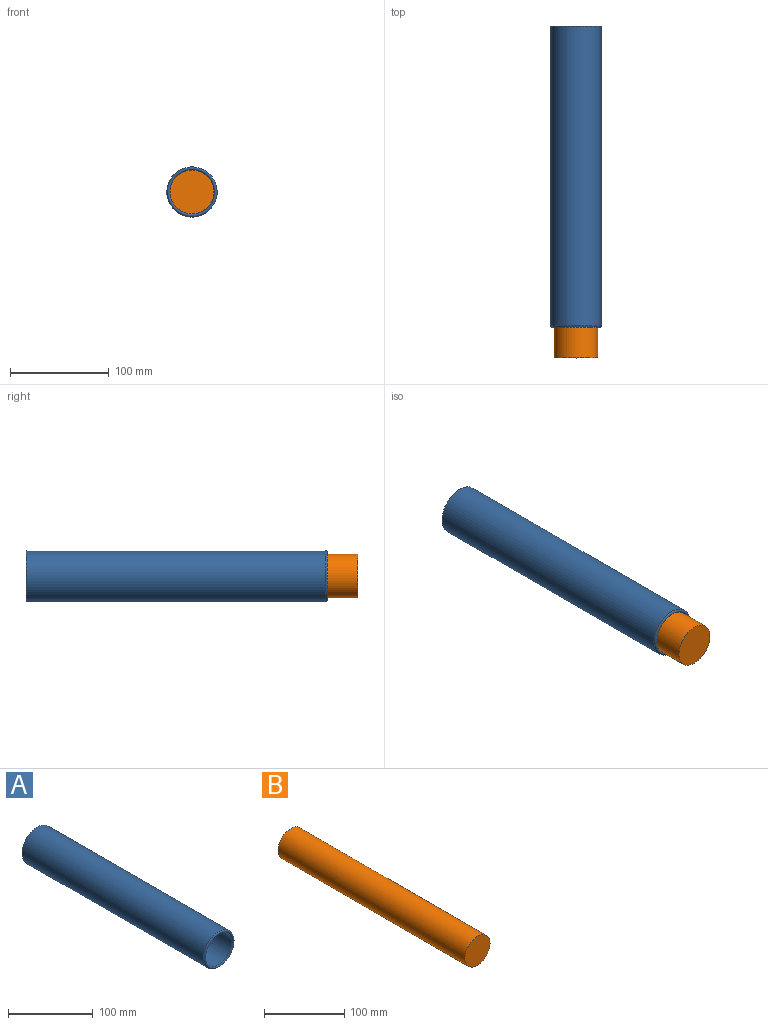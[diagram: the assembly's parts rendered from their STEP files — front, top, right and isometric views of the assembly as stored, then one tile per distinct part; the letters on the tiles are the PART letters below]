
ASSEMBLY  parts=2 mates=1
PART A: 5 faces, bbox 55x304.8x55 mm
  f0: cylinder r=22.23mm len=296.86mm, axis (0,1,0), area 41455mm2, adj f3,f4
  f1: cylinder r=25.4mm len=303.21mm, axis (0,1,0), area 48390.6mm2, adj f2,f4
  f2: plane 50.8x50.8mm, normal (0,1,0), area 2026.8mm2, adj f1
  f3: plane 44.45x44.45mm, normal (0,-1,0), area 1551.8mm2, adj f0
  f4: torus R=23.81mm, axis (0,-1,0), area 746.2mm2, adj f0,f1
PART B: 3 faces, bbox 44.5x330.2x44.5 mm
  f0: cylinder r=22.23mm len=330.2mm, axis (0,1,0), area 46110.4mm2, adj f1,f2
  f1: plane 44.45x44.45mm, normal (0,-1,0), area 1551.8mm2, adj f0
  f2: plane 44.45x44.45mm, normal (0,1,0), area 1551.8mm2, adj f0
PLACE A t=(36.19,-13.49,0.06)mm fixed
PLACE B t=(36.19,-19.05,0.06)mm
MATE slider A.f1 <-> B.f0  axis (0,1,0) through (36.19,-165.1,0.06)mm
